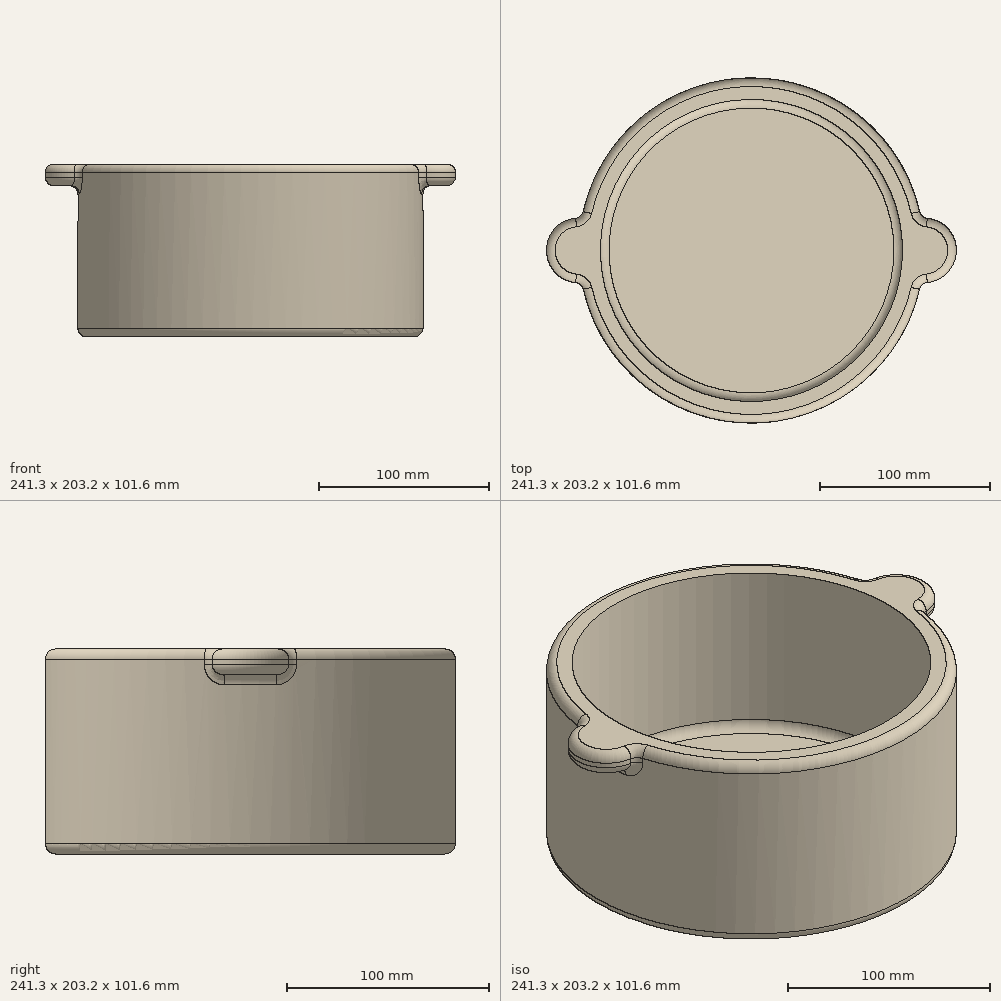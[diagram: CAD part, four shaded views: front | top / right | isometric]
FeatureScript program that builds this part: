
annotation { "Feature Type Name" : "Feature", "Feature Type Description" : "" }
export const myFeature = defineFeature(function(context is Context, id is Id, definition is map)
    precondition{}
    {
        {
            var Q0;
            Q0=qCreatedBy(makeId("Top.planeOp"),FACE);
            var sketch = newSketch(context, id + "F0", { "sketchPlane" : qUnion([Q0])});
            skCircle(sketch, "E0", {"center": v(0, 0) * mm, "radius": 96.84 * mm});
            skSolve(sketch);
        }
        {
            var Q0;
            Q0 = qSketchRegion(id + "F0", true);
            extrude(context, id + "F1", {"entities" : qUnion([Q0]), "depth" : 92.07 * mm, "offsetDistance" : 25.4 * mm});
        }
        {
            var Q0;
            Q0=makeQuery(id+"F1.opExtrude","CAP_FACE",FACE,{"disambiguationData":[OSD([sQuery(id+"F0.wireOp",EDGE,"E0")])],"isStart":false});
            var sketch = newSketch(context, id + "F2", { "sketchPlane" : qUnion([Q0])});
            skCircle(sketch, "E1", {"center": v(-96.84, 0) * mm, "radius": 19.05 * mm});
            skCircle(sketch, "E2", {"center": v(96.84, 0) * mm, "radius": 19.05 * mm});
            skSolve(sketch);
        }
        {
            var Q0;
            Q0 = qSketchRegion(id + "F2", true);
            extrude(context, id + "F3", {"entities" : qUnion([Q0]), "operationType" : NewBodyOperationType.ADD, "oppositeDirection" : true, "depth" : 12.7 * mm, "offsetDistance" : 25.4 * mm});
        }
        {
            var Q0;
            Q0=makeQuery(id+"F1.opExtrude","SWEPT_BODY",BODY,{"disambiguationData":[OSD([sQuery(id+"F0.wireOp",EDGE,"E0")])]});
            deleteBodies(context, id + "F4", {"entities" : qUnion([Q0])});
        }
        {
            var Q0;
            Q0=qCreatedBy(makeId("Top.planeOp"),FACE);
            var sketch = newSketch(context, id + "F5", { "sketchPlane" : qUnion([Q0])});
            skCircle(sketch, "E3", {"center": v(0, 0) * mm, "radius": 101.6 * mm});
            skSolve(sketch);
        }
        {
            var Q0;
            Q0 = qSketchRegion(id + "F5", true);
            extrude(context, id + "F6", {"entities" : qUnion([Q0]), "depth" : 101.6 * mm, "offsetDistance" : 25.4 * mm});
        }
        {
            var Q0;
            Q0=makeQuery(id+"F6.opExtrude","CAP_FACE",FACE,{"disambiguationData":[OSD([sQuery(id+"F5.wireOp",EDGE,"E3")])],"isStart":false});
            var sketch = newSketch(context, id + "F7", { "sketchPlane" : qUnion([Q0])});
            skCircle(sketch, "E4", {"center": v(101.6, 0) * mm, "radius": 19.05 * mm});
            skCircle(sketch, "E5", {"center": v(-101.6, 0) * mm, "radius": 19.05 * mm});
            skSolve(sketch);
        }
        {
            var Q0;
            Q0 = qSketchRegion(id + "F7", true);
            extrude(context, id + "F8", {"entities" : qUnion([Q0]), "operationType" : NewBodyOperationType.ADD, "oppositeDirection" : true, "depth" : 12.7 * mm, "offsetDistance" : 25.4 * mm});
        }
        {
            var Q0;
            Q0=makeQuery(id+"F8.boolean.opBoolean","MERGE",FACE,{"derivedFrom":[makeQuery(id+"F6.opExtrude","CAP_FACE",FACE,{"disambiguationData":[OSD([sQuery(id+"F5.wireOp",EDGE,"E3")])],"isStart":false}),makeQuery(id+"F8.opExtrude","CAP_FACE",FACE,{"disambiguationData":[OSD([sQuery(id+"F7.wireOp",EDGE,"E4")])],"isStart":true}),makeQuery(id+"F8.opExtrude","CAP_FACE",FACE,{"disambiguationData":[OSD([sQuery(id+"F7.wireOp",EDGE,"E5")])],"isStart":true})]});
            var sketch = newSketch(context, id + "F9", { "sketchPlane" : qUnion([Q0])});
            skCircle(sketch, "E6", {"center": v(0, 0) * mm, "radius": 88.9 * mm});
            skSolve(sketch);
        }
        {
            var Q0;
            Q0 = qSketchRegion(id + "F9", true);
            extrude(context, id + "F10", {"entities" : qUnion([Q0]), "operationType" : NewBodyOperationType.REMOVE, "oppositeDirection" : true, "depth" : 88.9 * mm, "offsetDistance" : 25.4 * mm});
        }
        {
            var Q0;
            Q0=makeQuery(id+"F8.boolean.opBoolean","SPLIT",EDGE,{"disambiguationData":[OD(0.0)],"derivedFrom":makeQuery(id+"F6.opExtrude","CAP_EDGE",EDGE,{"disambiguationData":[OSD([sQuery(id+"F5.wireOp",EDGE,"E3")])],"isStart":false})});
            var Q1;
            Q1=makeQuery(id+"F8.opExtrude","CAP_EDGE",EDGE,{"disambiguationData":[OSD([sQuery(id+"F7.wireOp",EDGE,"E5")])],"isStart":true});
            var Q2;
            Q2=makeQuery(id+"F8.boolean.opBoolean","SPLIT",EDGE,{"disambiguationData":[OD(1.0)],"derivedFrom":makeQuery(id+"F6.opExtrude","CAP_EDGE",EDGE,{"disambiguationData":[OSD([sQuery(id+"F5.wireOp",EDGE,"E3")])],"isStart":false})});
            var Q3;
            Q3=makeQuery(id+"F8.opExtrude","CAP_EDGE",EDGE,{"disambiguationData":[OSD([sQuery(id+"F7.wireOp",EDGE,"E4")])],"isStart":true});
            var Q4;
            Q4=makeQuery(id+"F8.opExtrude","CAP_EDGE",EDGE,{"disambiguationData":[OSD([sQuery(id+"F7.wireOp",EDGE,"E4")])],"isStart":false});
            var Q5;
            Q5=makeQuery(id+"F8.boolean.opBoolean","INTERSECT",EDGE,{"disambiguationData":[OD(0.0)],"derivedFrom":[makeQuery(id+"F6.opExtrude","SWEPT_FACE",FACE,{"disambiguationData":[OSD([sQuery(id+"F5.wireOp",EDGE,"E3")])]}),makeQuery(id+"F8.opExtrude","SWEPT_FACE",FACE,{"disambiguationData":[OSD([sQuery(id+"F7.wireOp",EDGE,"E4")])]})]});
            var Q6;
            Q6=makeQuery(id+"F8.boolean.opBoolean","INTERSECT",EDGE,{"disambiguationData":[OD(1.0)],"derivedFrom":[makeQuery(id+"F6.opExtrude","SWEPT_FACE",FACE,{"disambiguationData":[OSD([sQuery(id+"F5.wireOp",EDGE,"E3")])]}),makeQuery(id+"F8.opExtrude","SWEPT_FACE",FACE,{"disambiguationData":[OSD([sQuery(id+"F7.wireOp",EDGE,"E4")])]})]});
            var Q7;
            Q7=makeQuery(id+"F8.boolean.opBoolean","INTERSECT",EDGE,{"derivedFrom":[makeQuery(id+"F6.opExtrude","SWEPT_FACE",FACE,{"disambiguationData":[OSD([sQuery(id+"F5.wireOp",EDGE,"E3")])]}),makeQuery(id+"F8.opExtrude","CAP_FACE",FACE,{"disambiguationData":[OSD([sQuery(id+"F7.wireOp",EDGE,"E4")])],"isStart":false})]});
            var Q8;
            Q8=makeQuery(id+"F8.opExtrude","CAP_EDGE",EDGE,{"disambiguationData":[OSD([sQuery(id+"F7.wireOp",EDGE,"E5")])],"isStart":false});
            var Q9;
            Q9=makeQuery(id+"F8.boolean.opBoolean","INTERSECT",EDGE,{"derivedFrom":[makeQuery(id+"F6.opExtrude","SWEPT_FACE",FACE,{"disambiguationData":[OSD([sQuery(id+"F5.wireOp",EDGE,"E3")])]}),makeQuery(id+"F8.opExtrude","CAP_FACE",FACE,{"disambiguationData":[OSD([sQuery(id+"F7.wireOp",EDGE,"E5")])],"isStart":false})]});
            var Q10;
            Q10=makeQuery(id+"F8.boolean.opBoolean","INTERSECT",EDGE,{"disambiguationData":[OD(1.0)],"derivedFrom":[makeQuery(id+"F6.opExtrude","SWEPT_FACE",FACE,{"disambiguationData":[OSD([sQuery(id+"F5.wireOp",EDGE,"E3")])]}),makeQuery(id+"F8.opExtrude","SWEPT_FACE",FACE,{"disambiguationData":[OSD([sQuery(id+"F7.wireOp",EDGE,"E5")])]})]});
            var Q11;
            Q11=makeQuery(id+"F8.boolean.opBoolean","INTERSECT",EDGE,{"disambiguationData":[OD(0.0)],"derivedFrom":[makeQuery(id+"F6.opExtrude","SWEPT_FACE",FACE,{"disambiguationData":[OSD([sQuery(id+"F5.wireOp",EDGE,"E3")])]}),makeQuery(id+"F8.opExtrude","SWEPT_FACE",FACE,{"disambiguationData":[OSD([sQuery(id+"F7.wireOp",EDGE,"E5")])]})]});
            fillet(context, id + "F11", {"entities" : qUnion([Q0, Q1, Q2, Q3, Q4, Q5, Q6, Q7, Q8, Q9, Q10, Q11]), "radius" : 5.08 * mm, "tangentPropagation" : true, "allowEdgeOverflow" : false});
        }
        {
            var Q0;
            Q0=makeQuery(id+"F6.opExtrude","CAP_EDGE",EDGE,{"disambiguationData":[OSD([sQuery(id+"F5.wireOp",EDGE,"E3")])],"isStart":true});
            fillet(context, id + "F12", {"entities" : qUnion([Q0]), "radius" : 5.08 * mm, "tangentPropagation" : true, "allowEdgeOverflow" : false});
        }
        {
            var Q0;
            Q0=makeQuery(id+"F10.boolean.opBoolean","COPY",EDGE,{"derivedFrom":makeQuery(id+"F10.opExtrude","CAP_EDGE",EDGE,{"disambiguationData":[OSD([sQuery(id+"F9.wireOp",EDGE,"E6")])],"isStart":false})});
            fillet(context, id + "F13", {"entities" : qUnion([Q0]), "radius" : 5.08 * mm, "tangentPropagation" : true, "allowEdgeOverflow" : false});
        }
    });
